# Revit family: Haworth_BuzziTotem_Cylinder
name_source: partatom
category: Furniture
revit_build: Autodesk Revit 2018 (Build: 20170223_1515(x64)
units: mm (PartAtom-declared; Revit-internal decimal feet)

## family parameters
Always vertical = Yes
Cut with Voids When Loaded = No
OmniClass Number = 23.40.70.14.64.21
OmniClass Title = Systems Furniture
Room Calculation Point = No
Shared = No
Work Plane-Based = No

## types (3) — shared parameters
Assembly Code = E2020200
Casters = No
Manufacturer = Haworth
Model = HCBZ-TTS2
Revision Number = 1
Size = Verify Final Dim. w/ Haworth
URL = http://www.haworth.com
URL - Product = https://www.haworth.com
Warranty = http://www.haworth.com
zero-valued in all types: Actual Depth, Actual Height, Actual Width

## per-type parameters (varying)
| type | Description | Large | Medium | Small |
| HCBZ-TTS2-32 | Haworth BuzziTotem Cylinder Large | Yes | No | No |
| HCBZ-TTS2-22 | Haworth BuzziTotem Cylinder Medium | No | Yes | No |
| HCBZ-TTS2-12 | Haworth BuzziTotem Cylinder Small | No | No | Yes |

## geometry (parser evidence)
native form markers: Sweep x3
no freeform markers — native parametric forms only
